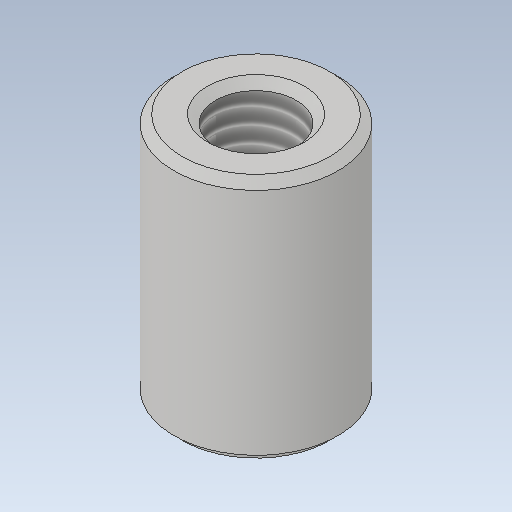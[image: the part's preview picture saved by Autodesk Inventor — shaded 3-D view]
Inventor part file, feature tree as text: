
AUTODESK INVENTOR PART (.ipt)
format: ipt  version: 2020.1 (Build 241239000, 239)  size: 115,200 bytes
history: native  units: mm
features: extrude x1, hole x1, chamfer x1, sketch x1
ambient origin geometry x8: Origin, YZ Plane, XZ Plane, XY Plane, X Axis, Y Axis, Z Axis, Center Point
bodies: Solid1 (feature_tree)
feature tree (4):
  extrude  "Extrusion1"  Depth=15.0mm TaperAngle=0.0deg
  hole  "Hole1"  [1 undecoded]
  chamfer  "Chamfer1"  [1 undecoded]
  sketch  "Sketch1"  dims[d0=10.0mm d1=15.0mm d2=0.0mm d12=10.0mm d13=10.0mm d5=4.917mm d6=12.0mm d7=4.0mm d8=2.0mm d9=90.0deg d10=17.1mm d11=20.594885mm d14=0.5mm d15=2.0mm d16=45.0deg]
note: 2 required parameter values undecoded (feature->parameter linkage not recoverable at this tier; creation-order binding heuristic only, values carry confidence <= 0.55)
